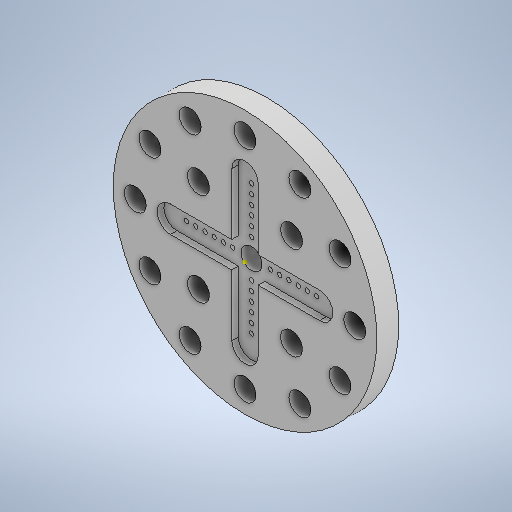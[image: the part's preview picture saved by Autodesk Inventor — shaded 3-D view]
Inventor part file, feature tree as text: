
AUTODESK INVENTOR PART (.ipt)
format: ipt  version: 2025.2 (Build 292293000, 293)  size: 399,360 bytes
history: native  units: mm
features: sketch x12, extrude x8, pattern_circular x3, other x2, hole x1
ambient origin geometry x8: Origin, YZ Plane, XZ Plane, XY Plane, X Axis, Y Axis, Z Axis, Center Point
bodies: Body1 (feature_tree)
feature tree (26):
  other  "Bryła1"
  extrude  "Wyciągnięcie proste1"  Depth=60.0mm
  sketch  "Szkic3"
  extrude  "Wyciągnięcie proste2"  Depth=5.0mm TaperAngle=0.0deg
  sketch  "Szkic7"
  extrude  "Wyciągnięcie proste3"  Depth=4.8mm
  extrude  "Wyciągnięcie proste4"  Depth=5.0mm TaperAngle=0.0deg
  pattern_circular  "Szyk kołowy1"  [2 undecoded]
  hole  "Otwór2"  [1 undecoded]
  pattern_circular  "Szyk kołowy2"  [2 undecoded]
  extrude  "Wyciągnięcie proste8"  Depth=120.0mm TaperAngle=360.0deg
  extrude  "Wyciągnięcie proste9"  Depth=5.0mm TaperAngle=0.0deg
  extrude  "Wyciągnięcie proste10"  Depth=5.0mm
  pattern_circular  "Szyk kołowy3"  [2 undecoded]
  extrude  "Wyciągnięcie proste11"  Depth=120.0mm TaperAngle=360.0deg
  sketch  "Szkic27"
  sketch  "Szkic1"
  sketch  "Szkic4"
  sketch  "Szkic11"
  other  "Kołowy szyk szkicu1"
  sketch  "Szkic16"
  sketch  "Szkic22"
  sketch  "Szkic23"
  sketch  "Szkic24"
  sketch  "Szkic25"
  sketch  "Szkic26"
note: 7 required parameter values undecoded (feature->parameter linkage not recoverable at this tier; creation-order binding heuristic only, values carry confidence <= 0.55)
